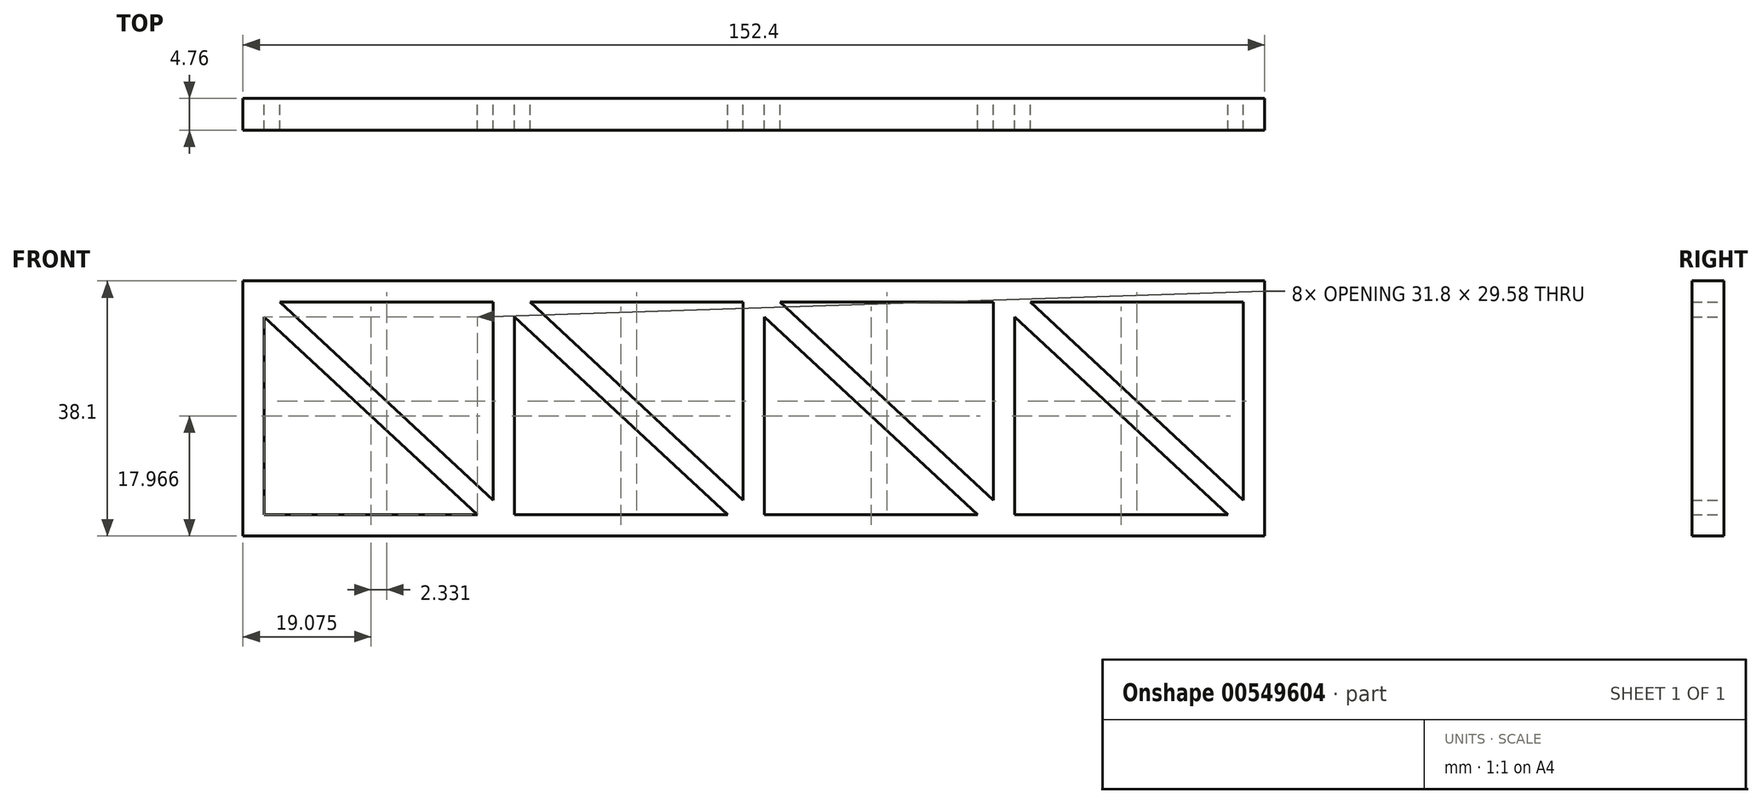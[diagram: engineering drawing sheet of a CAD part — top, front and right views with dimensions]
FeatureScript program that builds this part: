
annotation { "Feature Type Name" : "Feature", "Feature Type Description" : "" }
export const myFeature = defineFeature(function(context is Context, id is Id, definition is map)
    precondition{}
    {
        {
            var Q0;
            Q0=qCreatedBy(makeId("Front.planeOp"),FACE);
            var sketch = newSketch(context, id + "F0", { "sketchPlane" : qUnion([Q0])});
            skLineSegment(sketch, "E0.bottom", {"start": v(-76.2, 19.05) * mm, "end": v(76.2, 19.05) * mm});
            skLineSegment(sketch, "E0.top", {"start": v(-76.2, -19.05) * mm, "end": v(76.2, -19.05) * mm});
            skLineSegment(sketch, "E0.left", {"start": v(-76.2, 19.05) * mm, "end": v(-76.2, -19.05) * mm});
            skLineSegment(sketch, "E0.right", {"start": v(76.2, 19.05) * mm, "end": v(76.2, -19.05) * mm});
            skPoint(sketch, "E0.middle", {"position": v(0, 0) * mm});
            skLineSegment(sketch, "E1.0", {"start": v(-70.7, 15.87) * mm, "end": v(-38.9, 15.87) * mm});
            skLineSegment(sketch, "E1.1", {"start": v(-73.03, 13.7) * mm, "end": v(-73.03, -15.87) * mm});
            skLineSegment(sketch, "E1.2", {"start": v(-73.03, -15.87) * mm, "end": v(-41.22, -15.87) * mm});
            skLineSegment(sketch, "E1.3", {"start": v(73.03, 15.87) * mm, "end": v(73.03, -13.7) * mm});
            skLineSegment(sketch, "E2.left", {"start": v(-1.59, 15.88) * mm, "end": v(-1.59, -13.7) * mm});
            skLineSegment(sketch, "E2.right", {"start": v(1.59, 13.7) * mm, "end": v(1.59, -15.88) * mm});
            skLineSegment(sketch, "E3.trimOffspring", {"start": v(3.92, 15.87) * mm, "end": v(35.72, 15.87) * mm});
            skLineSegment(sketch, "E4.trimOffspring", {"start": v(1.59, -15.87) * mm, "end": v(33.39, -15.87) * mm});
            skLineSegment(sketch, "E5", {"start": v(0, 19.05) * mm, "end": v(0, -19.05) * mm, "construction": true});
            skLineSegment(sketch, "E6", {"start": v(-37.3, 15.87) * mm, "end": v(-37.3, -15.87) * mm, "construction": true});
            skLineSegment(sketch, "E7", {"start": v(37.3, 15.87) * mm, "end": v(37.3, -15.87) * mm, "construction": true});
            skLineSegment(sketch, "E8.0.left", {"start": v(-35.72, 13.7) * mm, "end": v(-35.72, -15.87) * mm});
            skLineSegment(sketch, "E8.0.right", {"start": v(-38.9, 15.87) * mm, "end": v(-38.9, -13.7) * mm});
            skLineSegment(sketch, "E9.0.left", {"start": v(38.9, 13.7) * mm, "end": v(38.9, -15.87) * mm});
            skLineSegment(sketch, "E9.0.right", {"start": v(35.72, 15.87) * mm, "end": v(35.72, -13.7) * mm});
            skLineSegment(sketch, "E10", {"start": v(-73.03, 15.88) * mm, "end": v(-38.9, -15.87) * mm, "construction": true});
            skLineSegment(sketch, "E11", {"start": v(-35.72, 15.87) * mm, "end": v(-1.59, -15.87) * mm, "construction": true});
            skLineSegment(sketch, "E12", {"start": v(1.59, 15.87) * mm, "end": v(35.72, -15.87) * mm, "construction": true});
            skLineSegment(sketch, "E13", {"start": v(38.9, 15.87) * mm, "end": v(73.03, -15.87) * mm, "construction": true});
            skLineSegment(sketch, "E14.trimOffspring", {"start": v(41.22, 15.87) * mm, "end": v(73.03, 15.87) * mm});
            skLineSegment(sketch, "E15.trimOffspring", {"start": v(38.9, -15.87) * mm, "end": v(70.7, -15.87) * mm});
            skLineSegment(sketch, "E16.trimOffspring", {"start": v(-33.39, 15.87) * mm, "end": v(-1.59, 15.87) * mm});
            skLineSegment(sketch, "E17.trimOffspring", {"start": v(-35.72, -15.87) * mm, "end": v(-3.92, -15.87) * mm});
            skLineSegment(sketch, "E18.0.left", {"start": v(-70.7, 15.88) * mm, "end": v(-38.9, -13.7) * mm});
            skLineSegment(sketch, "E18.0.right", {"start": v(-73.03, 13.7) * mm, "end": v(-41.22, -15.87) * mm});
            skLineSegment(sketch, "E18.1.left", {"start": v(-33.39, 15.87) * mm, "end": v(-1.59, -13.7) * mm});
            skLineSegment(sketch, "E18.1.right", {"start": v(-35.72, 13.7) * mm, "end": v(-3.92, -15.87) * mm});
            skLineSegment(sketch, "E18.2.left", {"start": v(3.92, 15.87) * mm, "end": v(35.72, -13.7) * mm});
            skLineSegment(sketch, "E18.2.right", {"start": v(1.59, 13.7) * mm, "end": v(33.39, -15.87) * mm});
            skLineSegment(sketch, "E18.3.left", {"start": v(41.22, 15.87) * mm, "end": v(73.02, -13.7) * mm});
            skLineSegment(sketch, "E18.3.right", {"start": v(38.9, 13.7) * mm, "end": v(70.7, -15.87) * mm});
            skSolve(sketch);
        }
        {
            var Q0;
            Q0 = qSketchRegion(id + "F0", true);
            extrude(context, id + "F1", {"entities" : qUnion([Q0]), "depth" : 4.76 * mm, "offsetDistance" : 25.4 * mm});
        }
    });
